# Revit family: 3475A_NXSW_SimpleTouch
name_source: partatom
category: Communication Devices
revit_build: Autodesk Revit 2014 (Build: 20130308_1515(x64)
units: mm (PartAtom-declared; Revit-internal decimal feet)

## types (1)
- 3475A_NXSW_SimpleTouch
    Apparent Load = 0 VA
    Assembly Code = D5090
    Default Elevation = 48 "
    Description = graphic wall station is an attractive and
capable user interface for a NX controlled space
    Features = Flexible, user friendly interface
• Customizable home screen and navigation
• 3.5” resistive LCD-TFT full color touch screen
• 320x480 screen resolution
• Mounts to a standard single gang switch box
• 4GB microSD card for storing user preferences up to 16 presets
• Single Cat5 connection to NX room system
• Up to 16 groups for on/off, dimming, or CCT control
• Allows playback of up to16 preset scenes
• Setup groups, presets, and schedules using linked Smart Device*
• Optional password access control
• Adjustable screensaver backlight
    Housing Material = Glass, White, High Luminance
    Inuput Power = 130 mA
    Inuput Voltage = 12 – 24 VDC
    Manufacturer = Hubbell Control Solutions
    Model = Graphic Wall Station
    Mounting = Single gang switch box or low voltage ring
    Product Documentation Link = https://hubbellcdn.com
    Product Page URL = https://www.hubbell.com
    Text = Metal-Hubbell-Aluminum Anodized Blue
    Type Comments = Graphic Wall Station
    URL = https://www.hubbell.com
    Warranty = 5-Years Warranty

## geometry (parser evidence)
native form markers: Sweep x1
no freeform markers — native parametric forms only
